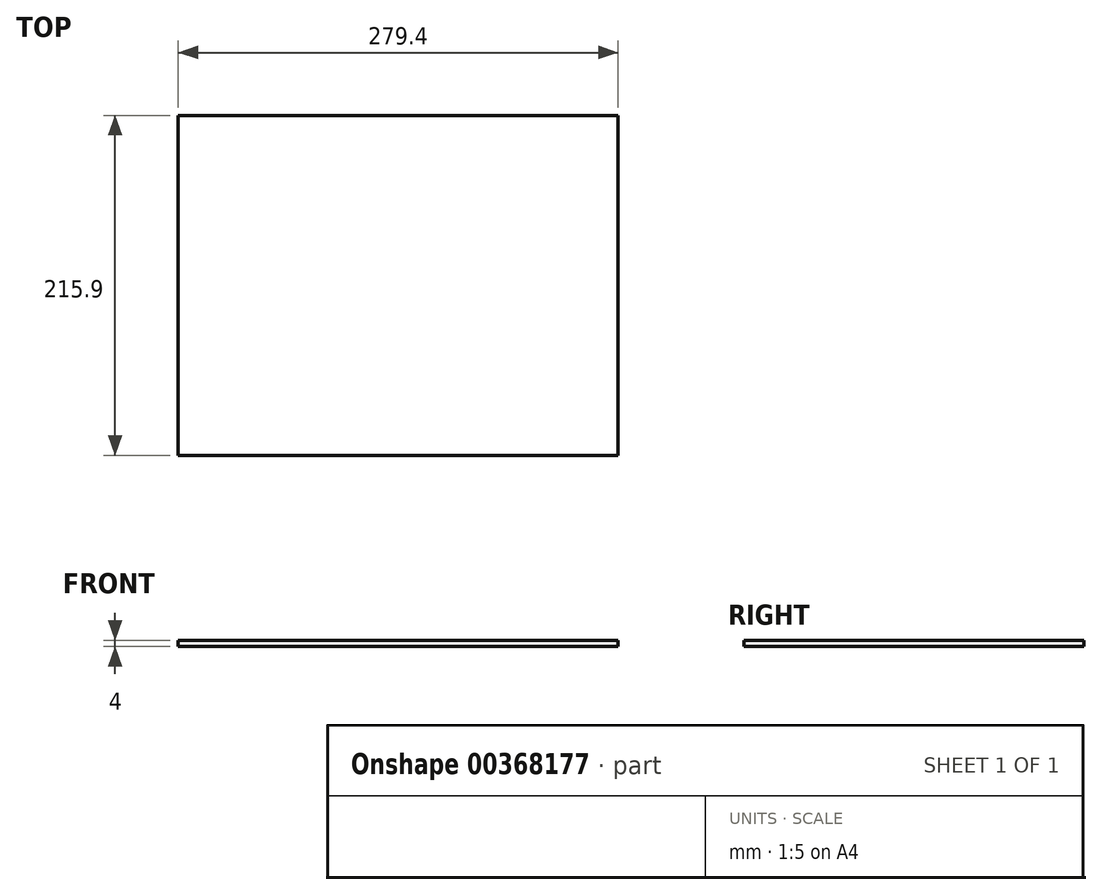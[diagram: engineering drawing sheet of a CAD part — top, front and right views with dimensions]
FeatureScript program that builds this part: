
annotation { "Feature Type Name" : "Feature", "Feature Type Description" : "" }
export const myFeature = defineFeature(function(context is Context, id is Id, definition is map)
    precondition{}
    {
        {
            var Q0;
            Q0=qCreatedBy(makeId("Top.planeOp"),FACE);
            var sketch = newSketch(context, id + "F0", { "sketchPlane" : qUnion([Q0])});
            skLineSegment(sketch, "E0.bottom", {"start": v(139.7, 107.95) * mm, "end": v(-139.7, 107.95) * mm});
            skLineSegment(sketch, "E0.top", {"start": v(139.7, -107.95) * mm, "end": v(-139.7, -107.95) * mm});
            skLineSegment(sketch, "E0.left", {"start": v(139.7, 107.95) * mm, "end": v(139.7, -107.95) * mm});
            skLineSegment(sketch, "E0.right", {"start": v(-139.7, 107.95) * mm, "end": v(-139.7, -107.95) * mm});
            skPoint(sketch, "E0.middle", {"position": v(0, 0) * mm});
            skSolve(sketch);
        }
        {
            var Q0;
            Q0=makeQuery(id+"F0.imprint","IMPRINT",FACE,{"disambiguationData":[TD([[makeQuery(id+"F0.imprint","IMPRINT",EDGE,{"derivedFrom":sQuery(id+"F0.wireOp",EDGE,"E0.bottom")}),1.0]])]});
            var Q1;
            Q1 = qSketchRegion(id + "FSBjJtPXkg0lhQz_0", true);
            extrude(context, id + "F1", {"entities" : qUnion([Q0, Q1]), "depth" : 4 * mm});
        }
    });
